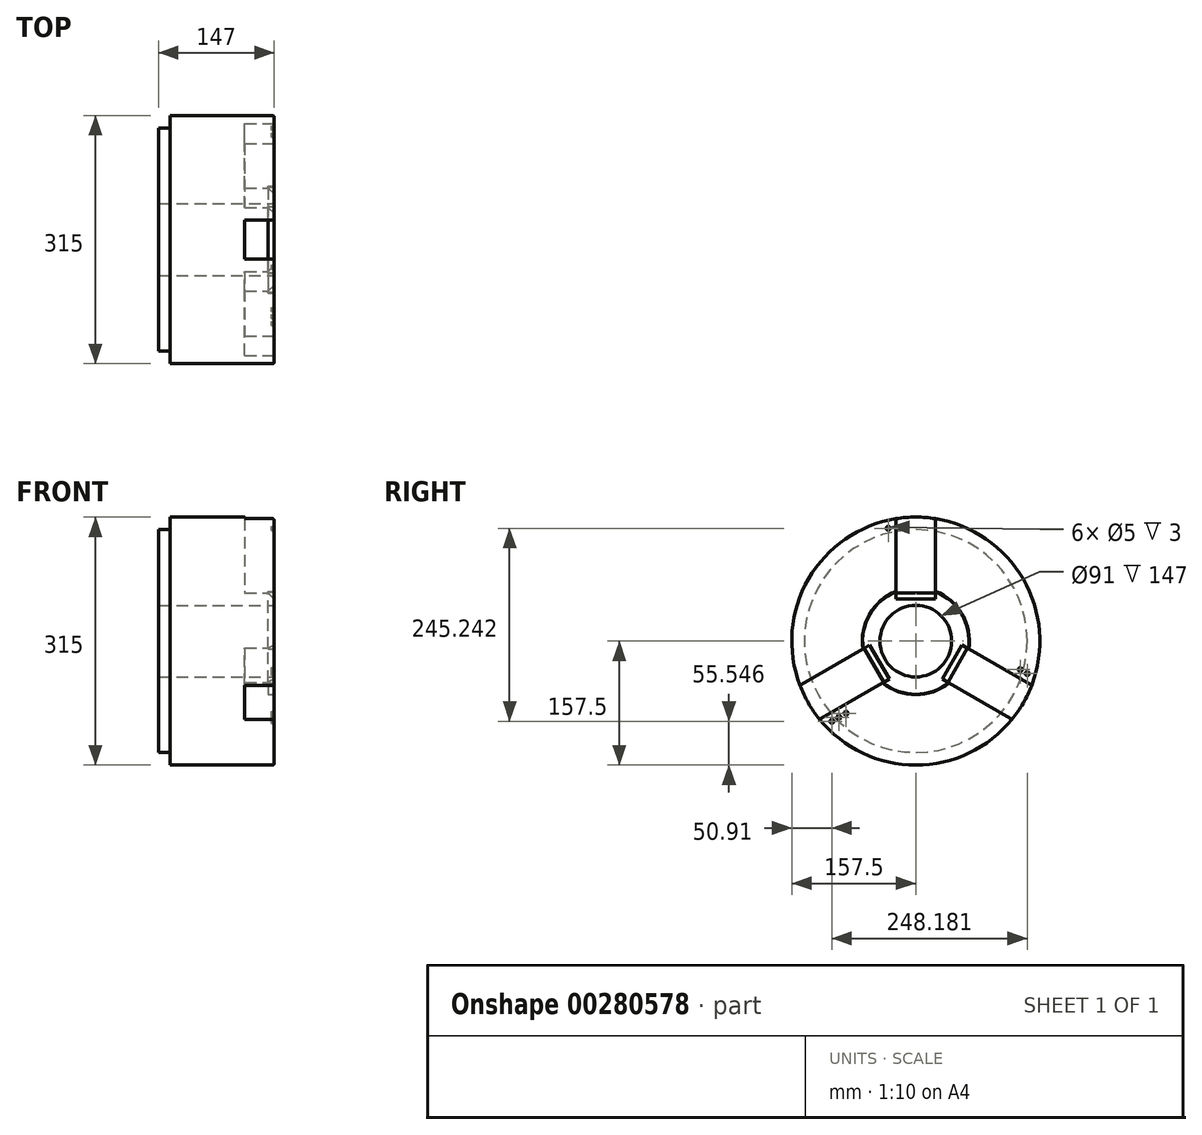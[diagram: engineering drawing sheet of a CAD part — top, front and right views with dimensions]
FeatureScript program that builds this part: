
annotation { "Feature Type Name" : "Feature", "Feature Type Description" : "" }
export const myFeature = defineFeature(function(context is Context, id is Id, definition is map)
    precondition{}
    {
        {
            var Q0;
            Q0=qCreatedBy(makeId("Front.planeOp"),FACE);
            var sketch = newSketch(context, id + "F0", { "sketchPlane" : qUnion([Q0])});
            skLineSegment(sketch, "E0", {"start": v(0, 45.5) * mm, "end": v(0, 67.5) * mm});
            skLineSegment(sketch, "E1", {"start": v(-2, 157.5) * mm, "end": v(-132, 157.5) * mm});
            skLineSegment(sketch, "E2", {"start": v(-132, 157.5) * mm, "end": v(-132, 141.5) * mm});
            skLineSegment(sketch, "E3", {"start": v(-132, 141.5) * mm, "end": v(-147, 141.5) * mm});
            skLineSegment(sketch, "E4", {"start": v(-147, 141.5) * mm, "end": v(-147, 45.5) * mm});
            skLineSegment(sketch, "E5", {"start": v(-147, 45.5) * mm, "end": v(0, 45.5) * mm});
            skLineSegment(sketch, "E6", {"start": v(294.82, 0) * mm, "end": v(-412.28, 0) * mm, "construction": true});
            skPoint(sketch, "E7.visualSharp", {"position": v(0, 157.5) * mm});
            skArc(sketch, "E7.filletArc", {"start": v(0, 155.5) * mm, "mid": v(-0.59, 156.91) * mm, "end": v(-2, 157.5) * mm});
            skLineSegment(sketch, "E8.bottom", {"start": v(0, 67.5) * mm, "end": v(-8, 67.5) * mm});
            skLineSegment(sketch, "E8.top", {"start": v(0, 68) * mm, "end": v(-8, 68) * mm});
            skLineSegment(sketch, "E8.right", {"start": v(-8, 67.5) * mm, "end": v(-8, 68) * mm});
            skLineSegment(sketch, "E9.trimOffspring", {"start": v(0, 68) * mm, "end": v(0, 155.5) * mm});
            skSolve(sketch);
        }
        {
            var Q0;
            Q0=qSketchRegion(id+"F0",true);
            var Q1;
            Q1=sQuery(id+"F0.wireOp",EDGE,"E6");
            revolve(context, id + "F1", {"entities" : qUnion([Q0]), "axis" : qUnion([Q1]), "revolveType" : RevolveType.FULL});
        }
        {
            var Q0;
            Q0=makeQuery(id+"F1.opRevolve","SWEPT_FACE",FACE,{"disambiguationData":[OSD([sQuery(id+"F0.wireOp",EDGE,"E0")])]});
            var sketch = newSketch(context, id + "F2", { "sketchPlane" : qUnion([Q0])});
            skLineSegment(sketch, "E10", {"start": v(0, 0) * mm, "end": v(0, 187.03) * mm, "construction": true});
            skArc(sketch, "E11", {"start": v(25, 155.5) * mm, "mid": v(0, 157.5) * mm, "end": v(-25, 155.5) * mm});
            skPoint(sketch, "E12", {"position": v(0, 62.16) * mm});
            skLineSegment(sketch, "E13", {"start": v(25, 155.5) * mm, "end": v(25, 60.5) * mm});
            skLineSegment(sketch, "E14", {"start": v(25, 60.5) * mm, "end": v(-25, 60.5) * mm});
            skLineSegment(sketch, "E15", {"start": v(-25, 60.5) * mm, "end": v(-25, 155.5) * mm});
            skSolve(sketch);
        }
        {
            var Q0;
            {var subQ0=sQuery(id+"F2.wireOp",EDGE,"E11");Q0=makeQuery(id+"F2.imprint","IMPRINT",FACE,{"disambiguationData":[TD([[makeQuery(id+"F2.imprint","IMPRINT",EDGE,{"derivedFrom":subQ0}),1.0]])]});}
            var Q1;
            {var subQ0=sQuery(id+"F2.wireOp",EDGE,"LmhPQE9t-ctvD-aCPM-Uwr9-EQLkLqq6skGc.bottom");Q1=makeQuery(id+"F2.imprint","IMPRINT",FACE,{"disambiguationData":[TD([[makeQuery(id+"F2.imprint","IMPRINT",EDGE,{"derivedFrom":subQ0}),-1.0]])]});}
            var Q2;
            {var subQ0=sQuery(id+"F2.wireOp",EDGE,"LmhPQE9t-ctvD-aCPM-Uwr9-EQLkLqq6skGc.bottom");var subQ1=makeQuery(id+"F1.opRevolve","SWEPT_EDGE",EDGE,{"disambiguationData":[OSD([sQuery(id+"F0.wireOp",EDGE,"E0"),sQuery(id+"F0.wireOp",EDGE,"E8.bottom")])]});var subQ2=makeQuery(id+"F2.imprint","INTERSECT",VERTEX,{"disambiguationData":[OD(0.0)],"derivedFrom":[subQ1,subQ0]});Q2=makeQuery(id+"F2.imprint","IMPRINT",FACE,{"disambiguationData":[TD([[makeQuery(id+"F2.imprint","IMPRINT",EDGE,{"disambiguationData":[TD([[subQ2,-1.0]])],"derivedFrom":subQ0}),-1.0]])]});}
            extrude(context, id + "F3", {"entities" : qUnion([Q0, Q1, Q2]), "operationType" : NewBodyOperationType.REMOVE, "oppositeDirection" : true, "depth" : 37.5 * mm});
        }
        {
            var Q0;
            Q0=makeQuery(id+"F1.opRevolve","SWEPT_FACE",FACE,{"disambiguationData":[OSD([sQuery(id+"F0.wireOp",EDGE,"E0")])]});
            var sketch = newSketch(context, id + "F4", { "sketchPlane" : qUnion([Q0])});
            skLineSegment(sketch, "E16", {"start": v(25, 73.3) * mm, "end": v(-25, 73.3) * mm});
            skLineSegment(sketch, "E17", {"start": v(-25, 73.3) * mm, "end": v(-25, 53.3) * mm});
            skLineSegment(sketch, "E18", {"start": v(-25, 53.3) * mm, "end": v(25, 53.3) * mm});
            skLineSegment(sketch, "E19", {"start": v(25, 53.3) * mm, "end": v(25, 73.3) * mm});
            skSolve(sketch);
        }
        {
            var Q0;
            Q0 = qSketchRegion(id + "F4", true);
            extrude(context, id + "F5", {"entities" : qUnion([Q0]), "operationType" : NewBodyOperationType.REMOVE, "oppositeDirection" : true, "depth" : 8 * mm});
        }
        {
            var Q0;
            Q0=makeQuery(id+"F5.boolean.opBoolean","COPY",EDGE,{"derivedFrom":makeQuery(id+"F5.opExtrude","CAP_EDGE",EDGE,{"disambiguationData":[OSD([sQuery(id+"F4.wireOp",EDGE,"E18")])],"isStart":false})});
            chamfer(context, id + "F6", {"entities" : qUnion([Q0]), "width" : 8 * mm, "tangentPropagation" : true});
        }
        {
            var Q0;
            Q0=makeQuery(id+"F5.boolean.opBoolean","COPY",FACE,{"derivedFrom":makeQuery(id+"F5.opExtrude","CAP_FACE",FACE,{"disambiguationData":[OSD([sQuery(id+"F4.wireOp",EDGE,"E16"),sQuery(id+"F4.wireOp",EDGE,"E17"),sQuery(id+"F4.wireOp",EDGE,"E18"),sQuery(id+"F4.wireOp",EDGE,"E19")])],"isStart":false})});
            var Q1;
            Q1=makeQuery(id+"F3.boolean.opBoolean","COPY",FACE,{"derivedFrom":makeQuery(id+"F3.opExtrude","CAP_FACE",FACE,{"disambiguationData":[OSD([sQuery(id+"F0.wireOp",EDGE,"E0"),sQuery(id+"F0.wireOp",EDGE,"E8.bottom"),sQuery(id+"F2.wireOp",EDGE,"E11"),sQuery(id+"F2.wireOp",EDGE,"E13"),sQuery(id+"F2.wireOp",EDGE,"E15")])],"isStart":false})});
            extrude(context, id + "F7", {"entities" : qUnion([Q0]), "operationType" : NewBodyOperationType.REMOVE, "endBound" : BoundingType.UP_TO_SURFACE, "oppositeDirection" : true, "endBoundEntityFace" : qUnion([Q1]), "depth" : 25 * mm});
        }
        {
            var Q0;
            Q0=makeQuery(id+"F6.opChamfer","BLEND_FACE",FACE,{"disambiguationData":[OSD([sQuery(id+"F4.wireOp",EDGE,"E18")])]});
            var Q1;
            {var subQ0=sQuery(id+"F4.wireOp",EDGE,"E19");Q1=makeQuery(id+"F7.boolean.opBoolean","MERGE",FACE,{"derivedFrom":[makeQuery(id+"F3.boolean.opBoolean","COPY",FACE,{"derivedFrom":makeQuery(id+"F3.opExtrude","SWEPT_FACE",FACE,{"disambiguationData":[OSD([sQuery(id+"F2.wireOp",EDGE,"E13")])]})}),makeQuery(id+"F5.boolean.opBoolean","COPY",FACE,{"derivedFrom":makeQuery(id+"F5.opExtrude","SWEPT_FACE",FACE,{"disambiguationData":[OSD([subQ0])]})})],"fromTools":[makeQuery(id+"F7.opExtrude","SWEPT_FACE",FACE,{"disambiguationData":[OSD([subQ0])]})]});}
            var Q2;
            Q2=makeQuery(id+"F7.boolean.opBoolean","COPY",FACE,{"derivedFrom":makeQuery(id+"F7.opExtrude","SWEPT_FACE",FACE,{"disambiguationData":[OSD([sQuery(id+"F4.wireOp",EDGE,"E16"),sQuery(id+"F4.wireOp",EDGE,"E17"),sQuery(id+"F4.wireOp",EDGE,"E18"),sQuery(id+"F4.wireOp",EDGE,"E19")])]})});
            var Q3;
            Q3=makeQuery(id+"F7.boolean.opBoolean","MERGE",FACE,{"derivedFrom":[makeQuery(id+"F3.boolean.opBoolean","COPY",FACE,{"derivedFrom":makeQuery(id+"F3.opExtrude","CAP_FACE",FACE,{"disambiguationData":[OSD([sQuery(id+"F0.wireOp",EDGE,"E0"),sQuery(id+"F0.wireOp",EDGE,"E8.bottom"),sQuery(id+"F2.wireOp",EDGE,"E11"),sQuery(id+"F2.wireOp",EDGE,"E13"),sQuery(id+"F2.wireOp",EDGE,"E15")])],"isStart":false})})],"fromTools":[makeQuery(id+"F7.opExtrude","CAP_FACE",FACE,{"disambiguationData":[OSD([sQuery(id+"F4.wireOp",EDGE,"E16"),sQuery(id+"F4.wireOp",EDGE,"E17"),sQuery(id+"F4.wireOp",EDGE,"E18"),sQuery(id+"F4.wireOp",EDGE,"E19")])],"isStart":false})]});
            var Q4;
            {var subQ0=sQuery(id+"F4.wireOp",EDGE,"E17");Q4=makeQuery(id+"F7.boolean.opBoolean","MERGE",FACE,{"derivedFrom":[makeQuery(id+"F3.boolean.opBoolean","COPY",FACE,{"derivedFrom":makeQuery(id+"F3.opExtrude","SWEPT_FACE",FACE,{"disambiguationData":[OSD([sQuery(id+"F2.wireOp",EDGE,"E15")])]})}),makeQuery(id+"F5.boolean.opBoolean","COPY",FACE,{"derivedFrom":makeQuery(id+"F5.opExtrude","SWEPT_FACE",FACE,{"disambiguationData":[OSD([subQ0])]})})],"fromTools":[makeQuery(id+"F7.opExtrude","SWEPT_FACE",FACE,{"disambiguationData":[OSD([subQ0])]})]});}
            var Q5;
            Q5=makeQuery(id+"F1.opRevolve","SWEPT_FACE",FACE,{"disambiguationData":[OSD([sQuery(id+"F0.wireOp",EDGE,"E5")])]});
            circularPattern(context, id + "F8", {"patternType" : PatternType.FACE, "operationType" : NewBodyOperationType.ADD, "faces" : qUnion([Q0, Q1, Q2, Q3, Q4]), "axis" : qUnion([Q5]), "angle" : 360 * degree, "instanceCount" : 3, "equalSpace" : true, "computeTransformsWithoutBuiltin" : true});
        }
        {
            var Q0;
            Q0=makeQuery(id+"F1.opRevolve","SWEPT_FACE",FACE,{"disambiguationData":[OSD([sQuery(id+"F0.wireOp",EDGE,"E0")])]});
            var sketch = newSketch(context, id + "F9", { "sketchPlane" : qUnion([Q0])});
            skCircle(sketch, "E20", {"center": v(-35, 143.29) * mm, "radius": 2.5 * mm});
            skCircle(sketch, "E21", {"center": v(0, 0) * mm, "radius": 147.5 * mm, "construction": true});
            skCircle(sketch, "E22", {"center": v(0, 0) * mm, "radius": 137.5 * mm, "construction": true});
            skCircle(sketch, "E23", {"center": v(0, 0) * mm, "radius": 127.5 * mm, "construction": true});
            skCircle(sketch, "E24", {"center": v(141.6, -41.33) * mm, "radius": 2.5 * mm});
            skCircle(sketch, "E25", {"center": v(132.66, -36.17) * mm, "radius": 2.5 * mm});
            skCircle(sketch, "E26", {"center": v(-106.6, -101.95) * mm, "radius": 2.5 * mm});
            skCircle(sketch, "E27", {"center": v(-97.66, -96.8) * mm, "radius": 2.5 * mm});
            skCircle(sketch, "E28", {"center": v(-88.68, -91.61) * mm, "radius": 2.5 * mm});
            skLineSegment(sketch, "E29", {"start": v(-35, 143.29) * mm, "end": v(-35, 107.8) * mm, "construction": true});
            skLineSegment(sketch, "E30", {"start": v(0, 107.8) * mm, "end": v(0, 150.74) * mm, "construction": true});
            skCircle(sketch, "E31.MirrorC", {"center": v(35, 143.29) * mm, "radius": 2.5 * mm});
            skLineSegment(sketch, "E32", {"start": v(141.6, -41.33) * mm, "end": v(110.08, -23.14) * mm, "construction": true});
            skLineSegment(sketch, "E33", {"start": v(0, 0) * mm, "end": v(131.49, -75.91) * mm, "construction": true});
            skCircle(sketch, "E34.MirrorC", {"center": v(97.66, -96.8) * mm, "radius": 2.5 * mm});
            skCircle(sketch, "E35.MirrorC", {"center": v(106.6, -101.95) * mm, "radius": 2.5 * mm});
            skLineSegment(sketch, "E36", {"start": v(0, 0) * mm, "end": v(-132.86, -76.7) * mm, "construction": true});
            skLineSegment(sketch, "E37", {"start": v(-106.6, -101.95) * mm, "end": v(-83.53, -88.64) * mm, "construction": true});
            skCircle(sketch, "E38.MirrorC", {"center": v(-123.68, -31) * mm, "radius": 2.5 * mm});
            skCircle(sketch, "E39.MirrorC", {"center": v(-132.66, -36.17) * mm, "radius": 2.5 * mm});
            skCircle(sketch, "E40.MirrorC", {"center": v(-141.6, -41.33) * mm, "radius": 2.5 * mm});
            skSolve(sketch);
        }
        {
            var Q0;
            Q0=makeQuery(id+"F9.imprint","IMPRINT",FACE,{"disambiguationData":[TD([[makeQuery(id+"F9.imprint","IMPRINT",EDGE,{"derivedFrom":sQuery(id+"F9.wireOp",EDGE,"E40.MirrorC")}),-1.0]])]});
            var Q1;
            Q1=makeQuery(id+"F9.imprint","IMPRINT",FACE,{"disambiguationData":[TD([[makeQuery(id+"F9.imprint","IMPRINT",EDGE,{"derivedFrom":sQuery(id+"F9.wireOp",EDGE,"E39.MirrorC")}),-1.0]])]});
            var Q2;
            Q2=makeQuery(id+"F9.imprint","IMPRINT",FACE,{"disambiguationData":[TD([[makeQuery(id+"F9.imprint","IMPRINT",EDGE,{"derivedFrom":sQuery(id+"F9.wireOp",EDGE,"E38.MirrorC")}),-1.0]])]});
            var Q3;
            Q3=makeQuery(id+"F9.imprint","IMPRINT",FACE,{"disambiguationData":[TD([[makeQuery(id+"F9.imprint","IMPRINT",EDGE,{"derivedFrom":sQuery(id+"F9.wireOp",EDGE,"E28")}),1.0]])]});
            var Q4;
            Q4=makeQuery(id+"F9.imprint","IMPRINT",FACE,{"disambiguationData":[TD([[makeQuery(id+"F9.imprint","IMPRINT",EDGE,{"derivedFrom":sQuery(id+"F9.wireOp",EDGE,"E27")}),1.0]])]});
            var Q5;
            Q5=makeQuery(id+"F9.imprint","IMPRINT",FACE,{"disambiguationData":[TD([[makeQuery(id+"F9.imprint","IMPRINT",EDGE,{"derivedFrom":sQuery(id+"F9.wireOp",EDGE,"E26")}),1.0]])]});
            var Q6;
            Q6=makeQuery(id+"F9.imprint","IMPRINT",FACE,{"disambiguationData":[TD([[makeQuery(id+"F9.imprint","IMPRINT",EDGE,{"derivedFrom":sQuery(id+"F9.wireOp",EDGE,"E34.MirrorC")}),-1.0]])]});
            var Q7;
            Q7=makeQuery(id+"F9.imprint","IMPRINT",FACE,{"disambiguationData":[TD([[makeQuery(id+"F9.imprint","IMPRINT",EDGE,{"derivedFrom":sQuery(id+"F9.wireOp",EDGE,"E35.MirrorC")}),-1.0]])]});
            var Q8;
            Q8=makeQuery(id+"F9.imprint","IMPRINT",FACE,{"disambiguationData":[TD([[makeQuery(id+"F9.imprint","IMPRINT",EDGE,{"derivedFrom":sQuery(id+"F9.wireOp",EDGE,"E24")}),1.0]])]});
            var Q9;
            Q9=makeQuery(id+"F9.imprint","IMPRINT",FACE,{"disambiguationData":[TD([[makeQuery(id+"F9.imprint","IMPRINT",EDGE,{"derivedFrom":sQuery(id+"F9.wireOp",EDGE,"E25")}),1.0]])]});
            var Q10;
            Q10=makeQuery(id+"F9.imprint","IMPRINT",FACE,{"disambiguationData":[TD([[makeQuery(id+"F9.imprint","IMPRINT",EDGE,{"derivedFrom":sQuery(id+"F9.wireOp",EDGE,"E31.MirrorC")}),-1.0]])]});
            var Q11;
            Q11=makeQuery(id+"F9.imprint","IMPRINT",FACE,{"disambiguationData":[TD([[makeQuery(id+"F9.imprint","IMPRINT",EDGE,{"derivedFrom":sQuery(id+"F9.wireOp",EDGE,"E20")}),1.0]])]});
            var Q12;
            Q12=sQuery(id+"F9.wireOp",EDGE,"E20");
            var Q13;
            Q13=sQuery(id+"F9.wireOp",EDGE,"E31.MirrorC");
            var Q14;
            Q14=sQuery(id+"F9.wireOp",EDGE,"E25");
            var Q15;
            Q15=sQuery(id+"F9.wireOp",EDGE,"E24");
            var Q16;
            Q16=sQuery(id+"F9.wireOp",EDGE,"E35.MirrorC");
            var Q17;
            Q17=sQuery(id+"F9.wireOp",EDGE,"E34.MirrorC");
            var Q18;
            Q18=sQuery(id+"F9.wireOp",EDGE,"E28");
            var Q19;
            Q19=sQuery(id+"F9.wireOp",EDGE,"E27");
            var Q20;
            Q20=sQuery(id+"F9.wireOp",EDGE,"E26");
            var Q21;
            Q21=sQuery(id+"F9.wireOp",EDGE,"E38.MirrorC");
            var Q22;
            Q22=sQuery(id+"F9.wireOp",EDGE,"E39.MirrorC");
            var Q23;
            Q23=sQuery(id+"F9.wireOp",EDGE,"E40.MirrorC");
            extrude(context, id + "F10", {"entities" : qUnion([Q0, Q1, Q2, Q3, Q4, Q5, Q6, Q7, Q8, Q9, Q10, Q11]), "operationType" : NewBodyOperationType.REMOVE, "surfaceEntities" : qUnion([Q12, Q13, Q14, Q15, Q16, Q17, Q18, Q19, Q20, Q21, Q22, Q23]), "oppositeDirection" : true, "depth" : 3 * mm});
        }
    });
